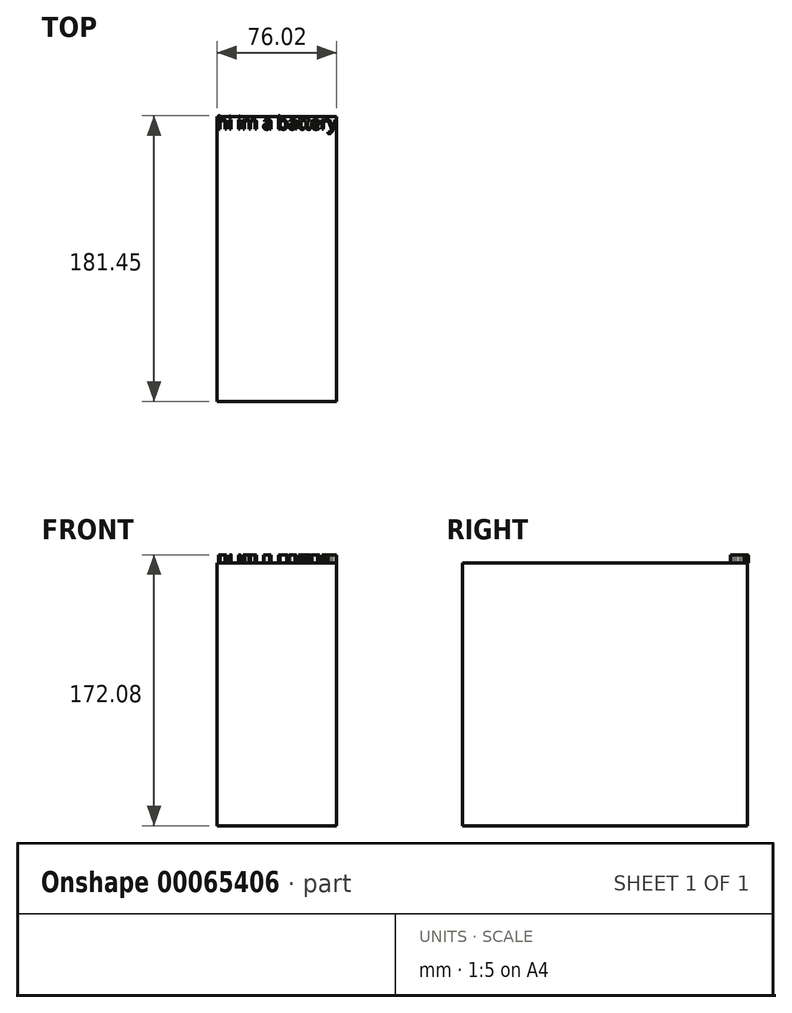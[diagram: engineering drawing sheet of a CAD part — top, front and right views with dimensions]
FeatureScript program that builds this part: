
annotation { "Feature Type Name" : "Feature", "Feature Type Description" : "" }
export const myFeature = defineFeature(function(context is Context, id is Id, definition is map)
    precondition{}
    {
        {
            var Q0;
            Q0=qCreatedBy(makeId("Front.planeOp"),FACE);
            var sketch = newSketch(context, id + "F0", { "sketchPlane" : qUnion([Q0])});
            skLineSegment(sketch, "E0.bottom", {"start": v(-47.06, 125.02) * mm, "end": v(28.94, 125.02) * mm});
            skLineSegment(sketch, "E0.top", {"start": v(-47.06, -41.98) * mm, "end": v(28.94, -41.98) * mm});
            skLineSegment(sketch, "E0.left", {"start": v(-47.06, 125.02) * mm, "end": v(-47.06, -41.98) * mm});
            skLineSegment(sketch, "E0.right", {"start": v(28.94, 125.02) * mm, "end": v(28.94, -41.98) * mm});
            skSolve(sketch);
        }
        {
            var Q0;
            Q0=makeQuery(id+"F0.imprint","IMPRINT",FACE,{"disambiguationData":[TD([[makeQuery(id+"F0.imprint","IMPRINT",EDGE,{"derivedFrom":sQuery(id+"F0.wireOp",EDGE,"E0.bottom")}),-1.0]])]});
            extrude(context, id + "F1", {"entities" : qUnion([Q0]), "depth" : 181 * mm});
        }
        {
            var Q0;
            Q0=makeQuery(id+"F1.opExtrude","SWEPT_FACE",FACE,{"disambiguationData":[OSD([sQuery(id+"F0.wireOp",EDGE,"E0.bottom")])]});
            var sketch = newSketch(context, id + "F2", { "sketchPlane" : qUnion([Q0])});
            skText(sketch, "E1", { "text": "hi im a battery", "fontName": "OpenSans-Regular.ttf"});
            const initialGuessF2  = {"E1": [-0.04706, -0.00813, 1, 0, 0.00813]};
            skSetInitialGuess(sketch, initialGuessF2);
            skSolve(sketch);
        }
        {
            var Q0;
            Q0 = qSketchRegion(id + "F2", true);
            extrude(context, id + "F3", {"entities" : qUnion([Q0]), "operationType" : NewBodyOperationType.ADD, "depth" : 5.08 * mm});
        }
    });
